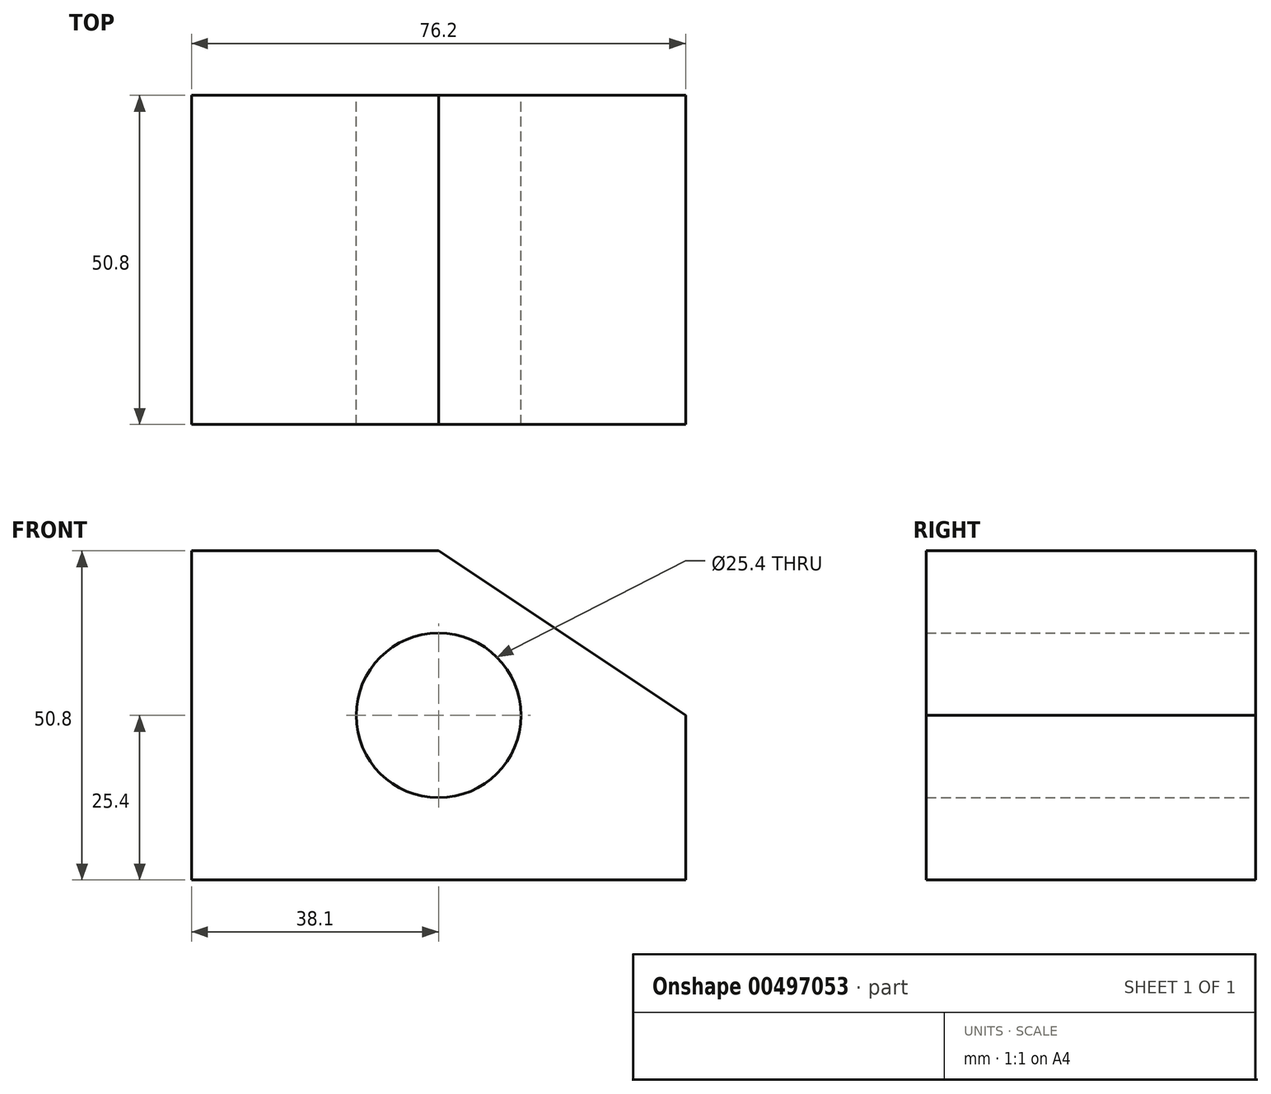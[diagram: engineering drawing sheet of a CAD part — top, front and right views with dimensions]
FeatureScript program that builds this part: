
annotation { "Feature Type Name" : "Feature", "Feature Type Description" : "" }
export const myFeature = defineFeature(function(context is Context, id is Id, definition is map)
    precondition{}
    {
        {
            var Q0;
            Q0=qCreatedBy(makeId("Front.planeOp"),FACE);
            var sketch = newSketch(context, id + "F0", { "sketchPlane" : qUnion([Q0])});
            skLineSegment(sketch, "E0.bottom", {"start": v(-19.05, 25.4) * mm, "end": v(19.05, 25.4) * mm});
            skLineSegment(sketch, "E0.top", {"start": v(-19.05, -25.4) * mm, "end": v(19.05, -25.4) * mm});
            skLineSegment(sketch, "E0.left", {"start": v(-19.05, 25.4) * mm, "end": v(-19.05, -25.4) * mm});
            skLineSegment(sketch, "E0.right", {"start": v(19.05, 25.4) * mm, "end": v(19.05, -25.4) * mm});
            skPoint(sketch, "E0.middle", {"position": v(0, 0) * mm});
            skLineSegment(sketch, "E1", {"start": v(19.05, -25.4) * mm, "end": v(57.15, -25.4) * mm});
            skLineSegment(sketch, "E2", {"start": v(57.15, -25.4) * mm, "end": v(57.15, 0) * mm});
            skLineSegment(sketch, "E3", {"start": v(57.15, 0) * mm, "end": v(19.05, 25.4) * mm});
            skCircle(sketch, "E4", {"center": v(19.05, 0) * mm, "radius": 12.7 * mm});
            skSolve(sketch);
        }
        {
            var Q0;
            {var subQ1=sQuery(id+"F0.wireOp",EDGE,"E0.bottom");Q0=makeQuery(id+"F0.imprint","IMPRINT",FACE,{"disambiguationData":[TD([[makeQuery(id+"F0.imprint","IMPRINT",EDGE,{"derivedFrom":subQ1}),-1.0]])]});}
            var Q1;
            {var subQ0=sQuery(id+"F0.wireOp",EDGE,"E1");Q1=makeQuery(id+"F0.imprint","IMPRINT",FACE,{"disambiguationData":[TD([[makeQuery(id+"F0.imprint","IMPRINT",EDGE,{"derivedFrom":subQ0}),1.0]])]});}
            extrude(context, id + "F1", {"entities" : qUnion([Q0, Q1]), "depth" : 50.8 * mm});
        }
    });
